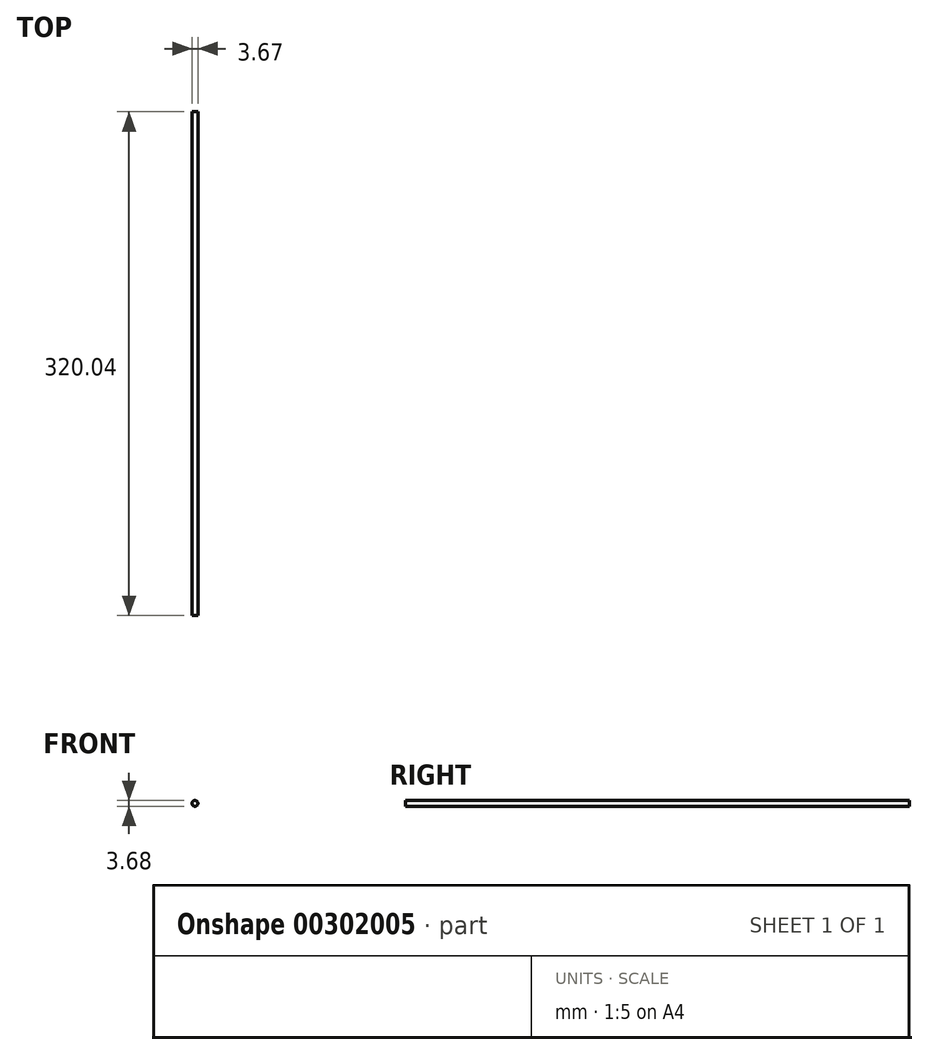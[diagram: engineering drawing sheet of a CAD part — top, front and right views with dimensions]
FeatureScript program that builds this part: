
annotation { "Feature Type Name" : "Feature", "Feature Type Description" : "" }
export const myFeature = defineFeature(function(context is Context, id is Id, definition is map)
    precondition{}
    {
        {
            var Q0;
            Q0=qCreatedBy(makeId("Front.planeOp"),FACE);
            var sketch = newSketch(context, id + "F0", { "sketchPlane" : qUnion([Q0])});
            skCircle(sketch, "E0", {"center": v(25.96, -6.65) * mm, "radius": 1.84 * mm});
            skSolve(sketch);
        }
        {
            var Q0;
            Q0 = qSketchRegion(id + "F0", true);
            extrude(context, id + "F1", {"entities" : qUnion([Q0]), "oppositeDirection" : true, "depth" : 320.04 * mm});
        }
    });
